# Revit family: S-756
name_source: partatom
category: Aparatos sanitarios
revit_build: Autodesk Revit 2015 (Build: 20140606_1530(x64)
units: mm (PartAtom-declared; Revit-internal decimal feet)

## types (6) — shared parameters
B = 52 mm
Comentarios de tipo = COMPATIBLE CON CERCOS VISTOS Y OCULTOS
Descripción = REJILLA PARA CANALETA, BUBBLE, PARA CANALETAS ANCHO 50
Fabricante = Jimten
Material = INOX AISI304
Modelo = S-756
Rejilla = INOX AISI304
URL = http://www.jimten.com

## per-type parameters (varying)
| type | A | Medida | N_MatrizHuecos | Referencia |
| 50x350mm_BUBBLE | 340 mm | 350mm x 50mm | 3 | 13539 |
| 50x550mm_BUBBLE | 540 mm | 550mm x 50mm | 5 | 13559 |
| 50x650mm_BUBBLE | 640 mm  [stored 2.09974 ft] | 650mm x 50mm | 6 | 13569 |
| 50x750mm_BUBBLE | 740 mm | 750mm x 50mm | 7 | 13579 |
| 50x850mm_BUBBLE | 840 mm | 850mm x 50mm | 8 | 13589 |
| 50x950mm_BUBBLE | 940 mm | 950mm x 50mm | 9 | 13599 |

note: [stored X ft] marks values corroborated as IEEE doubles in the binary element streams (Revit-internal decimal feet)

## geometry (parser evidence)
native form markers: Blend x3, Sweep x1
no freeform markers — native parametric forms only
